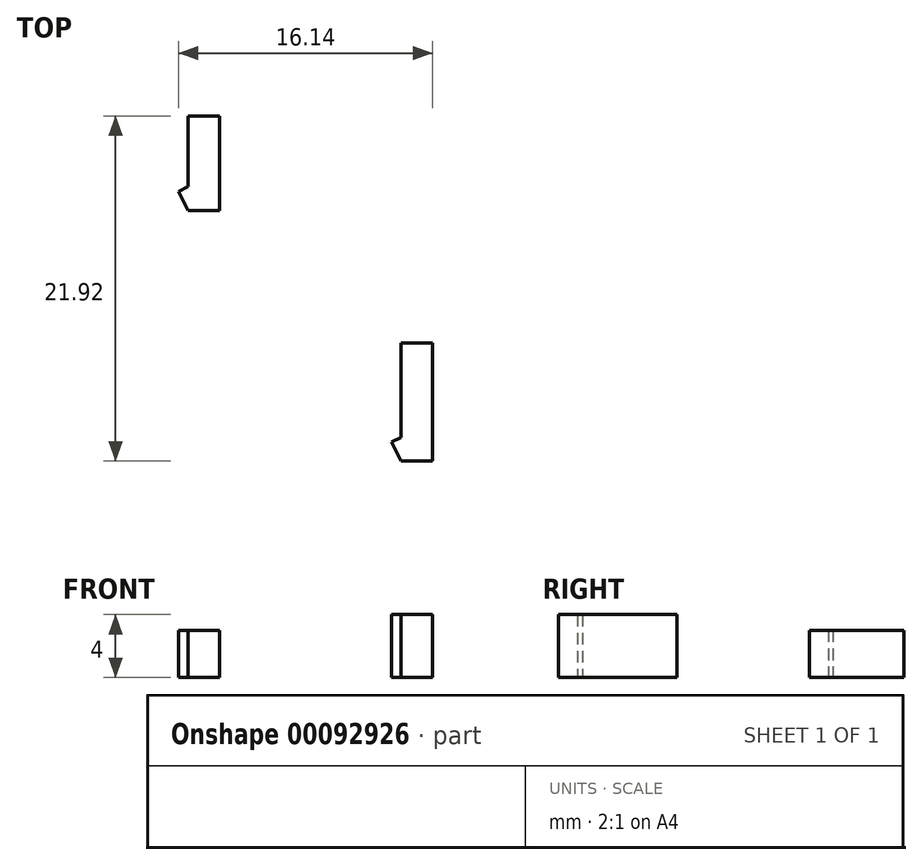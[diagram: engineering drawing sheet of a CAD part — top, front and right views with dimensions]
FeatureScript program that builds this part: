
annotation { "Feature Type Name" : "Feature", "Feature Type Description" : "" }
export const myFeature = defineFeature(function(context is Context, id is Id, definition is map)
    precondition{}
    {
        {
            var Q0;
            Q0=qCreatedBy(makeId("Top.planeOp"),FACE);
            var sketch = newSketch(context, id + "F0", { "sketchPlane" : qUnion([Q0])});
            skLineSegment(sketch, "E0.bottom", {"start": v(-2.01, 4.14) * mm, "end": v(-0.01, 4.14) * mm});
            skLineSegment(sketch, "E0.top", {"start": v(-2.01, -3.36) * mm, "end": v(-0.01, -3.36) * mm});
            skLineSegment(sketch, "E0.left", {"start": v(-2.01, 4.14) * mm, "end": v(-2.01, -1.86) * mm});
            skLineSegment(sketch, "E0.right", {"start": v(-0.01, 4.14) * mm, "end": v(-0.01, -3.36) * mm});
            skLineSegment(sketch, "E1", {"start": v(-2.01, -3.36) * mm, "end": v(-2.6, -2.15) * mm});
            skLineSegment(sketch, "E2", {"start": v(-2.6, -2.15) * mm, "end": v(-2.01, -1.86) * mm});
            skSolve(sketch);
        }
        {
            var Q0;
            Q0=makeQuery(id+"F0.imprint","IMPRINT",FACE,{"disambiguationData":[TD([[makeQuery(id+"F0.imprint","IMPRINT",EDGE,{"derivedFrom":sQuery(id+"F0.wireOp",EDGE,"E0.bottom")}),-1.0]])]});
            extrude(context, id + "F1", {"entities" : qUnion([Q0]), "depth" : 4 * mm});
        }
        {
            var Q0;
            Q0=qCreatedBy(makeId("Top.planeOp"),FACE);
            var sketch = newSketch(context, id + "F2", { "sketchPlane" : qUnion([Q0])});
            skLineSegment(sketch, "E3.bottom", {"start": v(-15.55, 18.56) * mm, "end": v(-13.55, 18.56) * mm});
            skLineSegment(sketch, "E3.top", {"start": v(-15.55, 12.56) * mm, "end": v(-13.55, 12.56) * mm});
            skLineSegment(sketch, "E3.left", {"start": v(-15.55, 18.56) * mm, "end": v(-15.55, 14.06) * mm});
            skLineSegment(sketch, "E3.right", {"start": v(-13.55, 18.56) * mm, "end": v(-13.55, 12.56) * mm});
            skLineSegment(sketch, "E4", {"start": v(-15.55, 12.56) * mm, "end": v(-16.15, 13.77) * mm});
            skLineSegment(sketch, "E5", {"start": v(-16.15, 13.77) * mm, "end": v(-15.55, 14.06) * mm});
            skPoint(sketch, "E6", {"position": v(-15.55, 15.56) * mm});
            skSolve(sketch);
        }
        {
            var Q0;
            Q0 = qSketchRegion(id + "F2", true);
            extrude(context, id + "F3", {"entities" : qUnion([Q0]), "depth" : 3 * mm});
        }
    });
